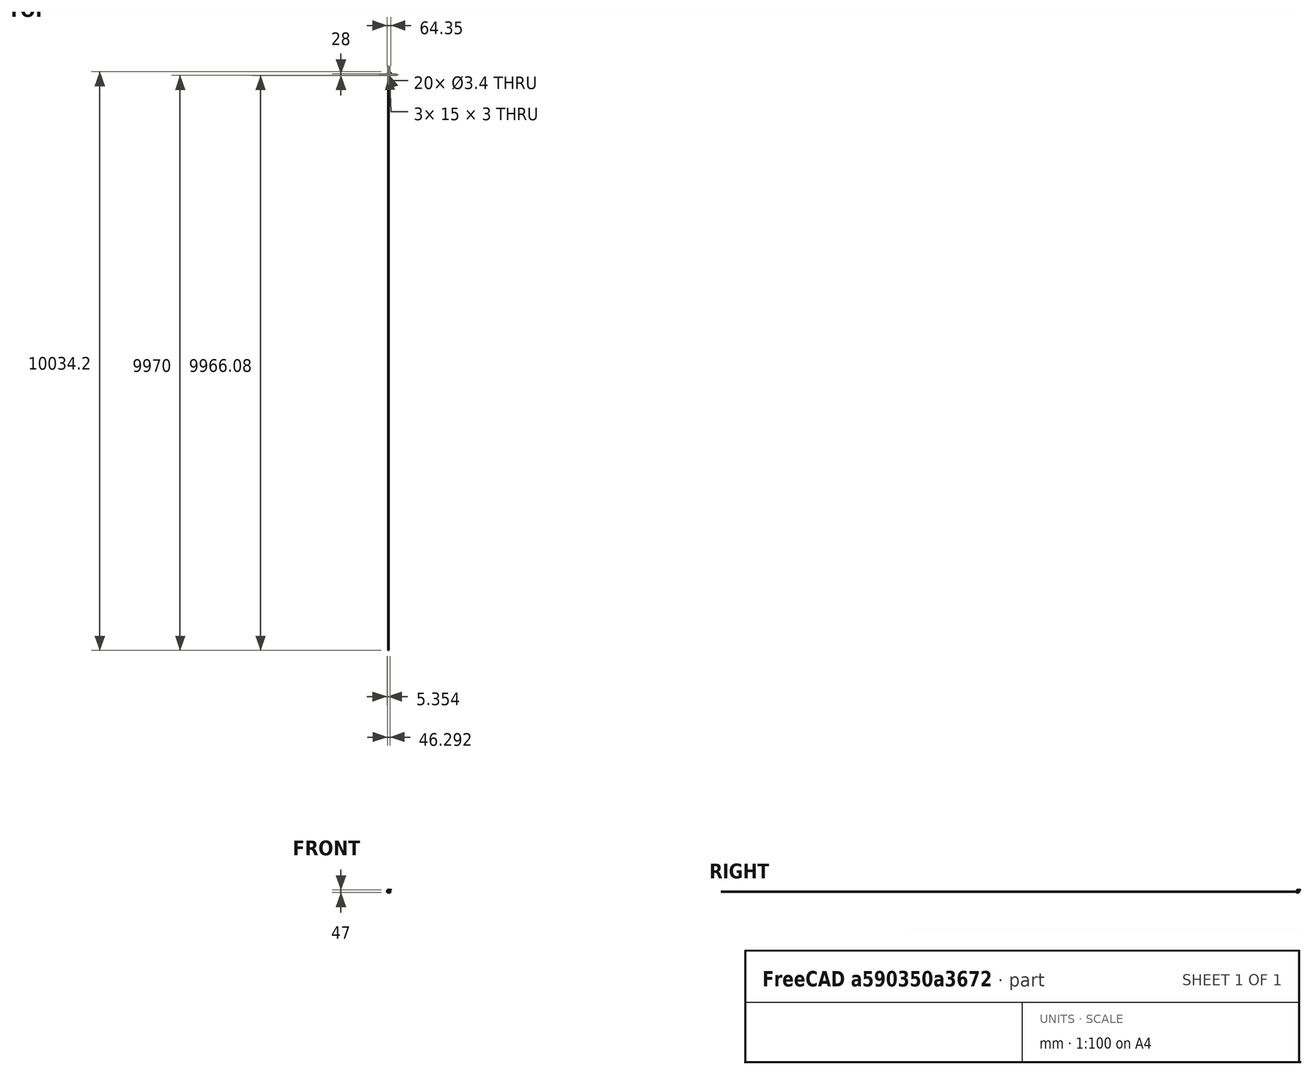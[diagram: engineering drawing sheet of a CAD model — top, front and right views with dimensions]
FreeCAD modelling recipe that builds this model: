
FCSTD DOCUMENT  (FreeCAD 0.14R2935 (Git))
Label: cabeza_v2
License: CC-BY 3.0
LicenseURL: http://creativecommons.org/licenses/by/3.0/
objects: Sketcher::SketchObject×22, PartDesign::Pocket×15, PartDesign::Pad×8, PartDesign::Chamfer×8, PartDesign::Fillet×6, App::DocumentObjectGroup×5, Part::Box×4, Part::FeaturePython×3, Part::Feature×3, Part::Cylinder×1, Mesh::Feature×1, Part::Cut×1
note: 94 computed .brp shape members not serialized (recipe doc carries the construction recipe); baked Part::Feature solids carry a one-line shape summary decoded from their .brp

FEATURE [Part::Box] Box
  Height = 2
  Length = 10
  Width = 12
FEATURE [Sketcher::SketchObject] Sketch
  Placement = pos=(0,0,2) rot=(0,0,1;0rad)
  Support = -> Box [Face6]
  sketch-geometry (1):
    g0: Circle CenterX=4.90431 CenterY=7.27272 CenterZ=0 NormalX=0 NormalY=0 NormalZ=1 Radius=4.25
  constraints (1):
    c: Radius(g0) = 4.25
FEATURE [PartDesign::Pad] Pad
  Length = 2
  Length2 = 100
  Sketch = -> Sketch
  Type = 0
FEATURE [Sketcher::SketchObject] Sketch001
  ExternalGeometry = -> [Pad]
  Placement = pos=(0,0,4) rot=(0,0,1;0rad)
  Support = -> Pad [Face8]
  sketch-geometry (1):
    g0: Circle CenterX=4.90431 CenterY=7.27272 CenterZ=0 NormalX=0 NormalY=0 NormalZ=1 Radius=2
  constraints (2):
    c: Coincident(g0,g-3)
    c: Radius(g0) = 2
FEATURE [PartDesign::Pocket] Pocket  label="camara"
  Length = 1
  Sketch = -> Sketch001
  Type = 0
FEATURE [App::DocumentObjectGroup] Grupo  label="Camera"
  Group = -> [Box,Pad,Pocket]
FEATURE [Part::FeaturePython] Clone  label="camara001"  # Draft clone (typed FeaturePython)
  Objects = -> [Pocket]
  Placement = pos=(1.5,0,-16) rot=(0,0,1;0rad)
  Scale = (1,1,1)
FEATURE [Part::Cylinder] Cylinder
  Angle = 360
  Height = 2
  Radius = 11.5
FEATURE [Sketcher::SketchObject] Sketch002
  Placement = pos=(0,0,2) rot=(0,0,1;0rad)
  Support = -> Cylinder [Face2]
  sketch-geometry (6):
    g0: LineSegment StartX=-3 StartY=3 StartZ=0 EndX=3 EndY=3 EndZ=0
    g1: LineSegment StartX=3 StartY=3 StartZ=0 EndX=3 EndY=-3 EndZ=0
    g2: LineSegment StartX=3 StartY=-3 StartZ=0 EndX=-3 EndY=-3 EndZ=0
    g3: LineSegment StartX=-3 StartY=-3 StartZ=0 EndX=-3 EndY=3 EndZ=0
    g4: LineSegment [constr] StartX=-3 StartY=3 StartZ=0 EndX=3 EndY=-3 EndZ=0
    g5: LineSegment [constr] StartX=3 StartY=3 StartZ=0 EndX=-3 EndY=-3 EndZ=0
  constraints (16):
    c: Coincident(g0,g1)
    c: Coincident(g1,g2)
    c: Coincident(g2,g3)
    c: Coincident(g3,g0)
    c: Horizontal(g0)
    c: Horizontal(g2)
    c: Vertical(g1)
    c: Vertical(g3)
    c: Equal(g0,g1)
    c: DistanceX(g2) = -6
    c: Coincident(g5,g0)
    c: Coincident(g5,g2)
    c: Coincident(g4,g1)
    c: Coincident(g4,g0)
    c: PointOnObject(g-1,g5)
    c: PointOnObject(g-1,g4)
FEATURE [PartDesign::Pad] Pad001
  Length = 1
  Length2 = 100
  Sketch = -> Sketch002
  Type = 0
FEATURE [Sketcher::SketchObject] Sketch003
  Placement = pos=(0,0,3) rot=(0,0,1;0rad)
  Support = -> Pad001 [Face8]
  sketch-geometry (1):
    g0: Circle CenterX=0 CenterY=0 CenterZ=0 NormalX=0 NormalY=0 NormalZ=1 Radius=2
  constraints (2):
    c: Coincident(g0,g-1)
    c: Radius(g0) = 2
FEATURE [PartDesign::Pocket] Pocket001
  Length = 1
  Sketch = -> Sketch003
  Type = 0
FEATURE [Sketcher::SketchObject] Sketch004
  ExternalGeometry = -> [Pocket001]
  Placement = pos=(0,0,2) rot=(0,0,1;0rad)
  Support = -> Pocket001 [Face2]
  sketch-geometry (28):
    g0: LineSegment StartX=-3 StartY=9.7 StartZ=0 EndX=3 EndY=9.7 EndZ=0
    g1: LineSegment StartX=3 StartY=9.7 StartZ=0 EndX=3 EndY=3.7 EndZ=0
    g2: LineSegment StartX=3 StartY=3.7 StartZ=0 EndX=-3 EndY=3.7 EndZ=0
    g3: LineSegment StartX=-3 StartY=3.7 StartZ=0 EndX=-3 EndY=9.7 EndZ=0
    g4: LineSegment StartX=-9.7 StartY=3 StartZ=0 EndX=-3.7 EndY=3 EndZ=0
    g5: LineSegment StartX=-3.7 StartY=3 StartZ=0 EndX=-3.7 EndY=-3 EndZ=0
    g6: LineSegment StartX=-3.7 StartY=-3 StartZ=0 EndX=-9.7 EndY=-3 EndZ=0
    g7: LineSegment StartX=-9.7 StartY=-3 StartZ=0 EndX=-9.7 EndY=3 EndZ=0
    g8: LineSegment StartX=-3 StartY=-3.7 StartZ=0 EndX=3 EndY=-3.7 EndZ=0
    g9: LineSegment StartX=3 StartY=-3.7 StartZ=0 EndX=3 EndY=-9.7 EndZ=0
    g10: LineSegment StartX=3 StartY=-9.7 StartZ=0 EndX=-3 EndY=-9.7 EndZ=0
    g11: LineSegment StartX=-3 StartY=-9.7 StartZ=0 EndX=-3 EndY=-3.7 EndZ=0
    g12: LineSegment StartX=3.7 StartY=3 StartZ=0 EndX=9.7 EndY=3 EndZ=0
    g13: LineSegment StartX=9.7 StartY=3 StartZ=0 EndX=9.7 EndY=-3 EndZ=0
    g14: LineSegment StartX=9.7 StartY=-3 StartZ=0 EndX=3.7 EndY=-3 EndZ=0
    g15: LineSegment StartX=3.7 StartY=-3 StartZ=0 EndX=3.7 EndY=3 EndZ=0
    g16: LineSegment [constr] StartX=-3 StartY=9.7 StartZ=0 EndX=3 EndY=3.7 EndZ=0
    g17: LineSegment [constr] StartX=3 StartY=9.7 StartZ=0 EndX=-3 EndY=3.7 EndZ=0
    g18: LineSegment [constr] StartX=3.7 StartY=3 StartZ=0 EndX=9.7 EndY=-3 EndZ=0
    g19: LineSegment [constr] StartX=9.7 StartY=3 StartZ=0 EndX=3.7 EndY=-3 EndZ=0
    g20: LineSegment [constr] StartX=-9.7 StartY=3 StartZ=0 EndX=-3.7 EndY=-3 EndZ=0
    g21: LineSegment [constr] StartX=-3.7 StartY=3 StartZ=0 EndX=-9.7 EndY=-3 EndZ=0
    g22: LineSegment [constr] StartX=-3 StartY=-3.7 StartZ=0 EndX=3 EndY=-9.7 EndZ=0
    g23: LineSegment [constr] StartX=3 StartY=-3.7 StartZ=0 EndX=-3 EndY=-9.7 EndZ=0
    g24: GeomPoint [constr] X=0 Y=-6.7 Z=0
    g25: GeomPoint [constr] X=6.7 Y=0 Z=0
    g26: GeomPoint [constr] X=-6.7 Y=0 Z=0
    g27: GeomPoint [constr] X=0 Y=6.7 Z=0
  constraints (72):
    c: Coincident(g0,g1)
    c: Coincident(g1,g2)
    c: Coincident(g2,g3)
    c: Coincident(g3,g0)
    c: Horizontal(g0)
    c: Horizontal(g2)
    c: Vertical(g1)
    c: Vertical(g3)
    c: Equal(g3,g2)
    c: Equal(g2,g-3)
    c: Coincident(g4,g5)
    c: Coincident(g5,g6)
    c: Coincident(g6,g7)
    c: Coincident(g7,g4)
    c: Horizontal(g4)
    c: Horizontal(g6)
    c: Vertical(g5)
    c: Vertical(g7)
    c: Coincident(g8,g9)
    c: Coincident(g9,g10)
    c: Coincident(g10,g11)
    c: Coincident(g11,g8)
    c: Horizontal(g8)
    c: Horizontal(g10)
    c: Vertical(g9)
    c: Vertical(g11)
    c: Coincident(g12,g13)
    c: Coincident(g13,g14)
    c: Coincident(g14,g15)
    c: Coincident(g15,g12)
    c: Horizontal(g12)
    c: Horizontal(g14)
    c: Vertical(g13)
    c: Vertical(g15)
    c: Equal(g12,g15)
    c: Equal(g15,g8)
    c: Equal(g8,g9)
    c: Equal(g9,g6)
    c: Equal(g6,g5)
    c: Equal(g2,g12)
    c: Coincident(g23,g10)
    c: Coincident(g22,g8)
    c: Coincident(g23,g8)
    c: Coincident(g22,g9)
    c: PointOnObject(g24,g-2)
    c: PointOnObject(g24,g23)
    c: PointOnObject(g24,g22)
    c: Coincident(g19,g12)
    c: Coincident(g18,g13)
    c: Coincident(g18,g12)
    c: Coincident(g19,g14)
    c: Coincident(g16,g1)
    c: Coincident(g17,g0)
    c: Coincident(g17,g2)
    c: Coincident(g16,g0)
    c: Coincident(g21,g4)
    c: Coincident(g20,g4)
    c: Coincident(g21,g6)
    c: Coincident(g20,g5)
    c: PointOnObject(g25,g-1)
    c: PointOnObject(g26,g-1)
    c: PointOnObject(g27,g-2)
    c: PointOnObject(g26,g20)
    c: PointOnObject(g26,g21)
    c: PointOnObject(g25,g19)
    c: PointOnObject(g25,g18)
    c: PointOnObject(g27,g16)
    c: PointOnObject(g27,g17)
    c: Distance(g-4,g4) = 0.7
    c: Distance(g-4,g8) = 0.7
    c: Distance(g-5,g14) = 0.7
    c: Distance(g2,g-4) = 0.7
FEATURE [PartDesign::Pad] Pad002
  Length = 1
  Length2 = 100
  Sketch = -> Sketch004
  Type = 0
FEATURE [Sketcher::SketchObject] Sketch005
  ExternalGeometry = -> [Pad002]
  Placement = pos=(0,0,3) rot=(0,0,1;0rad)
  Support = -> Pad002 [Face26]
  sketch-geometry (4):
    g0: Circle CenterX=0 CenterY=6.61559 CenterZ=0 NormalX=0 NormalY=0 NormalZ=1 Radius=2
    g1: Circle CenterX=-6.61558 CenterY=0 CenterZ=0 NormalX=0 NormalY=0 NormalZ=1 Radius=2
    g2: Circle CenterX=6.71215 CenterY=0 CenterZ=0 NormalX=0 NormalY=0 NormalZ=1 Radius=2
    g3: Circle CenterX=0 CenterY=-6.71214 CenterZ=0 NormalX=0 NormalY=0 NormalZ=1 Radius=2
  constraints (8):
    c: Equal(g1,g0)
    c: Equal(g0,g-3)
    c: Equal(g-3,g2)
    c: Equal(g2,g3)
    c: PointOnObject(g2,g-1)
    c: PointOnObject(g0,g-2)
    c: PointOnObject(g1,g-1)
    c: PointOnObject(g3,g-2)
FEATURE [PartDesign::Pocket] Pocket002
  Length = 1
  Sketch = -> Sketch005
  Type = 0
FEATURE [Part::FeaturePython] Clone001  label="ojo001"  # Draft clone (typed FeaturePython)
  Objects = -> [Pocket002]
  Placement = pos=(-7,-6,-13) rot=(0,0,1;0rad)
  Scale = (1,1,1)
FEATURE [App::DocumentObjectGroup] Grupo001  label="ojo"
  Group = -> [Cylinder,Pad001,Pocket001,Pad002,Pocket002]
FEATURE [Part::FeaturePython] Clone002  label="ojo002"  # Draft clone (typed FeaturePython)
  Objects = -> [Pocket002]
  Placement = pos=(21,-7,-13) rot=(0,0,1;0rad)
  Scale = (1,1,1)
FEATURE [Part::Box] Box001
  Height = 4
  Length = 35
  Placement = pos=(-11,-31,-17) rot=(0,0,1;0rad)
  Width = 47
FEATURE [Mesh::Feature] _g_servo  label="9g_servo"
  Placement = pos=(0,-7,-24) rot=(0.57735,0.57735,0.57735;2.0944rad)
FEATURE [Sketcher::SketchObject] Sketch006
  ExternalGeometry = -> [Box001]
  Placement = pos=(-11,-31,-17) rot=(1,0,0;3.14159rad)
  Support = -> Box001 [Face5]
  sketch-geometry (9):
    g0: LineSegment StartX=6.5 StartY=-7.91944 StartZ=0 EndX=13.302 EndY=-7.91944 EndZ=0
    g1: LineSegment StartX=13.302 StartY=-7.91944 StartZ=0 EndX=13.302 EndY=-11.9194 EndZ=0
    g2: LineSegment StartX=13.302 StartY=-11.9194 StartZ=0 EndX=6.5 EndY=-11.9194 EndZ=0
    g3: LineSegment StartX=6.5 StartY=-11.9194 StartZ=0 EndX=6.5 EndY=-7.91944 EndZ=0
    g4: LineSegment StartX=6.5 StartY=-35.9194 StartZ=0 EndX=13.302 EndY=-35.9194 EndZ=0
    g5: LineSegment StartX=13.302 StartY=-35.9194 StartZ=0 EndX=13.302 EndY=-39.9194 EndZ=0
    g6: LineSegment StartX=13.302 StartY=-39.9194 StartZ=0 EndX=6.5 EndY=-39.9194 EndZ=0
    g7: LineSegment StartX=6.5 StartY=-39.9194 StartZ=0 EndX=6.5 EndY=-35.9194 EndZ=0
    g8: LineSegment [constr] StartX=6.5 StartY=0 StartZ=0 EndX=6.5 EndY=-47 EndZ=0
  constraints (27):
    c: Coincident(g0,g1)
    c: Coincident(g1,g2)
    c: Coincident(g2,g3)
    c: Coincident(g3,g0)
    c: Horizontal(g0)
    c: Horizontal(g2)
    c: Vertical(g1)
    c: Vertical(g3)
    c: Coincident(g4,g5)
    c: Coincident(g5,g6)
    c: Coincident(g6,g7)
    c: Coincident(g7,g4)
    c: Horizontal(g4)
    c: Horizontal(g6)
    c: Vertical(g5)
    c: Vertical(g7)
    c: Equal(g2,g4)
    c: Vertical(g8)
    c: PointOnObject(g8,g-3)
    c: PointOnObject(g8,g-1)
    c: PointOnObject(g0,g8)
    c: PointOnObject(g4,g8)
    c: Equal(g1,g5)
    c: DistanceY(g1) = -4
    c: Distance(g2,g4) = 24
    c: Distance(g6,g8) = 7.08056
    c: Distance(g-3,g8) = 6.5
FEATURE [PartDesign::Pad] Pad003
  Length = 14
  Length2 = 100
  Placement = pos=(-11,-31,-17) rot=(0,0,1;0rad)
  Sketch = -> Sketch006
  Type = 0
FEATURE [Sketcher::SketchObject] Sketch007
  ExternalGeometry = -> [Pad003]
  Placement = pos=(2.30204,-31,-17) rot=(0.57735,0.57735,0.57735;2.0944rad)
  Support = -> Pad003 [Face7]
  sketch-geometry (3):
    g0: Circle CenterX=9.93523 CenterY=-7.03791 CenterZ=0 NormalX=0 NormalY=0 NormalZ=1 Radius=1.64716
    g1: Circle CenterX=37.8885 CenterY=-7.03791 CenterZ=0 NormalX=0 NormalY=0 NormalZ=1 Radius=1.53113
    g2: LineSegment [constr] StartX=35.9194 StartY=-7.03791 StartZ=0 EndX=11.9194 EndY=-7.03791 EndZ=0
  constraints (5):
    c: PointOnObject(g2,g-3)
    c: Horizontal(g2)
    c: PointOnObject(g2,g-4)
    c: PointOnObject(g0,g2)
    c: PointOnObject(g1,g2)
FEATURE [PartDesign::Pocket] Pocket003
  Length = 7
  Placement = pos=(-11,-31,-17) rot=(0,0,1;0rad)
  Sketch = -> Sketch007
  Type = 0
FEATURE [Sketcher::SketchObject] Sketch008
  ExternalGeometry = -> [Pocket003]
  Placement = pos=(-11,-31,-17) rot=(1,0,0;3.14159rad)
  Support = -> Pocket003 [Face5]
  sketch-geometry (6):
    g0: ArcOfCircle CenterX=31.6459 CenterY=-23.9498 CenterZ=0 NormalX=0 NormalY=0 NormalZ=1 Radius=11.5 StartAngle=5.00835 EndAngle=7.55802
    g1: LineSegment [constr] StartX=35 StartY=-12.9498 StartZ=0 EndX=0 EndY=-12.9498 EndZ=0
    g2: LineSegment [constr] StartX=35 StartY=-34.9498 StartZ=0 EndX=0 EndY=-34.9498 EndZ=0
    g3: ArcOfCircle CenterX=3.3541 CenterY=-23.9498 CenterZ=0 NormalX=0 NormalY=0 NormalZ=1 Radius=11.5 StartAngle=1.86676 EndAngle=4.41643
    g4: LineSegment StartX=35 StartY=-12.9498 StartZ=0 EndX=35 EndY=-34.9498 EndZ=0
    g5: LineSegment StartX=0 StartY=-12.9498 StartZ=0 EndX=0 EndY=-34.9498 EndZ=0
  constraints (20):
    c: PointOnObject(g0,g-3)
    c: PointOnObject(g0,g-3)
    c: Distance(g0,g0) = 22
    c: Radius(g0) = 11.5
    c: Horizontal(g1)
    c: Horizontal(g2)
    c: Distance(g-3,g0) = 12.9498
    c: Coincident(g1,g0)
    c: PointOnObject(g1,g-2)
    c: Coincident(g2,g0)
    c: PointOnObject(g2,g-2)
    c: Coincident(g3,g2)
    c: Coincident(g3,g1)
    c: Equal(g0,g3)
    c: Vertical(g4)
    c: Coincident(g4,g0)
    c: Coincident(g4,g0)
    c: Vertical(g5)
    c: Coincident(g5,g1)
    c: Coincident(g5,g2)
FEATURE [PartDesign::Pad] Pad004
  Length = 4
  Length2 = 100
  Placement = pos=(-11,-31,-17) rot=(0,0,1;0rad)
  Reversed = true
  Sketch = -> Sketch008
  Type = 0
FEATURE [Sketcher::SketchObject] Sketch009
  ExternalGeometry = -> [Pad004]
  Placement = pos=(-11,-31,-13) rot=(0,0,1;0rad)
  Support = -> Pad004 [Face4]
  sketch-geometry (6):
    g0: Circle CenterX=17.5 CenterY=38.5843 CenterZ=0 NormalX=0 NormalY=0 NormalZ=1 Radius=4.5
    g1: LineSegment [constr] StartX=0 StartY=38.5843 StartZ=0 EndX=17.5 EndY=38.5843 EndZ=0
    g2: LineSegment [constr] StartX=17.5 StartY=38.5843 StartZ=0 EndX=35 EndY=38.5843 EndZ=0
    g3: Circle CenterX=-5.6459 CenterY=23.9498 CenterZ=0 NormalX=0 NormalY=0 NormalZ=1 Radius=1.7
    g4: Circle CenterX=40.6459 CenterY=23.9498 CenterZ=0 NormalX=0 NormalY=0 NormalZ=1 Radius=1.7
    g5: LineSegment [constr] StartX=-8.1459 StartY=23.9498 StartZ=0 EndX=43.1459 EndY=23.9498 EndZ=0
  constraints (19):
    c: Horizontal(g1)
    c: Horizontal(g2)
    c: PointOnObject(g1,g-2)
    c: PointOnObject(g2,g-3)
    c: Coincident(g2,g0)
    c: Coincident(g1,g0)
    c: Equal(g1,g2)
    c: Radius(g0) = 4.5
    c: DistanceY(g-1,g2) = 38.5843
    c: Horizontal(g5)
    c: PointOnObject(g5,g-5)
    c: PointOnObject(g5,g-4)
    c: PointOnObject(g3,g5)
    c: PointOnObject(g4,g5)
    c: Radius(g4) = 1.7
    c: Radius(g3) = 1.7
    c: Distance(g3,g5) = 2.5
    c: Distance(g4,g5) = 2.5
    c: PointOnObject(g-5,g5)
FEATURE [PartDesign::Pocket] Pocket004
  Length = 4
  Placement = pos=(-11,-31,-17) rot=(0,0,1;0rad)
  Sketch = -> Sketch009
  Type = 0
FEATURE [Part::Feature] Pocket004001  label="Pocket005"
  shape: bbox 51.29 x 47 x 18 mm, 26 faces (baked)
FEATURE [PartDesign::Chamfer] Chamfer
  Base = -> Pocket004001 [Edge6]
  Size = 10
FEATURE [PartDesign::Chamfer] Chamfer001
  Base = -> Chamfer [Edge3]
  Size = 10
FEATURE [PartDesign::Fillet] Fillet
  Base = -> Chamfer001 [Edge3]
  Radius = 10
FEATURE [PartDesign::Fillet] Fillet001
  Base = -> Fillet [Edge3]
  Radius = 10
FEATURE [PartDesign::Fillet] Fillet002
  Base = -> Fillet001 [Edge45]
  Radius = 3
FEATURE [PartDesign::Fillet] Fillet003
  Base = -> Fillet002 [Edge43]
  Radius = 3
FEATURE [PartDesign::Chamfer] Chamfer002
  Base = -> Fillet003 [Edge46]
  Size = 10
FEATURE [PartDesign::Chamfer] Chamfer003
  Base = -> Chamfer002 [Edge29]
  Size = 10
FEATURE [Sketcher::SketchObject] Sketch010
  ExternalGeometry = -> [Chamfer003]
  Placement = pos=(0,0,-13) rot=(0,0,1;0rad)
  Support = -> Chamfer003 [Face29]
  sketch-geometry (9):
    g0: LineSegment [constr] StartX=-16.6459 StartY=-7.0502 StartZ=0 EndX=29.6459 EndY=-7.0502 EndZ=0
    g1: Circle CenterX=3.3541 CenterY=-7.0502 CenterZ=0 NormalX=0 NormalY=0 NormalZ=1 Radius=1.7
    g2: Circle CenterX=9.6459 CenterY=-7.0502 CenterZ=0 NormalX=0 NormalY=0 NormalZ=1 Radius=1.7
    g3: LineSegment [constr] StartX=-1 StartY=-7.0502 StartZ=0 EndX=-1 EndY=-31 EndZ=0
    g4: LineSegment [constr] StartX=14 StartY=-7.0502 StartZ=0 EndX=14 EndY=-31 EndZ=0
    g5: LineSegment StartX=-1 StartY=-23.5 StartZ=0 EndX=14 EndY=-23.5 EndZ=0
    g6: LineSegment StartX=14 StartY=-23.5 StartZ=0 EndX=14 EndY=-26.5 EndZ=0
    g7: LineSegment StartX=14 StartY=-26.5 StartZ=0 EndX=-1 EndY=-26.5 EndZ=0
    g8: LineSegment StartX=-1 StartY=-26.5 StartZ=0 EndX=-1 EndY=-23.5 EndZ=0
  constraints (27):
    c: Horizontal(g0)
    c: Coincident(g0,g-4)
    c: Coincident(g0,g-3)
    c: PointOnObject(g1,g0)
    c: PointOnObject(g2,g0)
    c: Radius(g2) = 1.7
    c: Radius(g1) = 1.7
    c: Distance(g0,g1) = 20
    c: Distance(g2,g0) = 20
    c: Vertical(g3)
    c: Coincident(g3,g-5)
    c: PointOnObject(g3,g0)
    c: Vertical(g4)
    c: Coincident(g4,g-5)
    c: PointOnObject(g4,g0)
    c: Coincident(g5,g6)
    c: Coincident(g6,g7)
    c: Coincident(g7,g8)
    c: Coincident(g8,g5)
    c: Horizontal(g5)
    c: Horizontal(g7)
    c: Vertical(g6)
    c: Vertical(g8)
    c: DistanceY(g6) = -3
    c: PointOnObject(g7,g3)
    c: PointOnObject(g6,g4)
    c: Distance(g7,g3) = 4.5
FEATURE [PartDesign::Pocket] Pocket004002
  Length = 5
  Sketch = -> Sketch010
  Type = 0
FEATURE [Sketcher::SketchObject] Sketch011
  Placement = pos=(0,8.91944,0) rot=(0,0.707107,0.707107;3.14159rad)
  Support = -> Pocket004002 [Face18]
  sketch-geometry (4):
    g0: LineSegment StartX=-1.74892 StartY=-26.7435 StartZ=0 EndX=3.95108 EndY=-26.7435 EndZ=0
    g1: LineSegment StartX=3.95108 StartY=-26.7435 StartZ=0 EndX=3.95108 EndY=-29.3435 EndZ=0
    g2: LineSegment StartX=3.95108 StartY=-29.3435 StartZ=0 EndX=-1.74892 EndY=-29.3435 EndZ=0
    g3: LineSegment StartX=-1.74892 StartY=-29.3435 StartZ=0 EndX=-1.74892 EndY=-26.7435 EndZ=0
  constraints (10):
    c: Coincident(g0,g1)
    c: Coincident(g1,g2)
    c: Coincident(g2,g3)
    c: Coincident(g3,g0)
    c: Horizontal(g0)
    c: Horizontal(g2)
    c: Vertical(g1)
    c: Vertical(g3)
    c: DistanceY(g1) = -2.6
    c: DistanceX(g2) = -5.7
FEATURE [PartDesign::Pocket] Pocket004003
  Length = 5
  Sketch = -> Sketch011
  Type = 1
FEATURE [Sketcher::SketchObject] Sketch012
  ExternalGeometry = -> [Pocket004003]
  Placement = pos=(0,0,-31) rot=(1,0,0;3.14159rad)
  Support = -> Pocket004003 [Face37]
  sketch-geometry (6):
    g0: LineSegment [constr] StartX=-4.5 StartY=23.0806 StartZ=0 EndX=2.30204 EndY=19.0806 EndZ=0
    g1: LineSegment [constr] StartX=2.30204 StartY=23.0806 StartZ=0 EndX=-4.5 EndY=19.0806 EndZ=0
    g2: Circle CenterX=-1.09898 CenterY=21.0806 CenterZ=0 NormalX=0 NormalY=0 NormalZ=1 Radius=1.7
    g3: LineSegment [constr] StartX=-4.5 StartY=-4.91944 StartZ=0 EndX=2.30204 EndY=-8.91944 EndZ=0
    g4: LineSegment [constr] StartX=2.30204 StartY=-4.91944 StartZ=0 EndX=-4.5 EndY=-8.91944 EndZ=0
    g5: Circle CenterX=-1.09898 CenterY=-6.91944 CenterZ=0 NormalX=0 NormalY=0 NormalZ=1 Radius=1.7
  constraints (14):
    c: Coincident(g1,g-4)
    c: Coincident(g1,g-3)
    c: Coincident(g0,g-4)
    c: Coincident(g0,g-3)
    c: PointOnObject(g2,g1)
    c: PointOnObject(g2,g0)
    c: Radius(g2) = 1.7
    c: Coincident(g4,g-6)
    c: Coincident(g4,g-5)
    c: Coincident(g3,g-6)
    c: Coincident(g3,g-5)
    c: PointOnObject(g5,g4)
    c: PointOnObject(g5,g3)
    c: Radius(g5) = 1.7
FEATURE [PartDesign::Pocket] Pocket004004
  Length = 4
  Sketch = -> Sketch012
  Type = 0
FEATURE [Part::Box] Box002
  Height = 26
  Length = 36
  Placement = pos=(-12,-31,-43) rot=(0,0,1;0rad)
  Width = 47
FEATURE [PartDesign::Pocket] Pocket004005
  Length = 4
  Sketch = -> Sketch012
  Type = 0
FEATURE [Part::Feature] Pocket004006  label="cara"
  shape: bbox 51.29 x 47 x 18 mm, 50 faces (baked)
FEATURE [PartDesign::Fillet] Fillet004
  Base = -> Box002 [Edge7]
  Placement = pos=(-12,-31,-43) rot=(0,0,1;0rad)
  Radius = 17
FEATURE [PartDesign::Fillet] Fillet005
  Base = -> Fillet004 [Edge15]
  Placement = pos=(-12,-31,-43) rot=(0,0,1;0rad)
  Radius = 17
FEATURE [PartDesign::Chamfer] Chamfer004
  Base = -> Fillet005 [Edge16]
  Placement = pos=(-12,-31,-43) rot=(0,0,1;0rad)
  Size = 10
FEATURE [PartDesign::Chamfer] Chamfer005
  Base = -> Chamfer004 [Edge16]
  Placement = pos=(-12,-31,-43) rot=(0,0,1;0rad)
  Size = 10
FEATURE [Part::Box] Box003
  Height = 26
  Length = 36
  Placement = pos=(-12,-31,-43) rot=(0,0,1;0rad)
  Width = 10
FEATURE [Part::Cut] Cut
  Base = -> Chamfer005
  Tool = -> Box003
FEATURE [Sketcher::SketchObject] Sketch013
  ExternalGeometry = -> [Cut]
  Placement = pos=(0,-21,0) rot=(1,0,0;1.5708rad)
  Support = -> Cut [Face7]
  sketch-geometry (4):
    g0: LineSegment StartX=-9 StartY=-17 StartZ=0 EndX=21 EndY=-17 EndZ=0
    g1: LineSegment StartX=21 StartY=-17 StartZ=0 EndX=21 EndY=-40 EndZ=0
    g2: LineSegment StartX=21 StartY=-40 StartZ=0 EndX=-9 EndY=-40 EndZ=0
    g3: LineSegment StartX=-9 StartY=-40 StartZ=0 EndX=-9 EndY=-17 EndZ=0
  constraints (12):
    c: Coincident(g0,g1)
    c: Coincident(g1,g2)
    c: Coincident(g2,g3)
    c: Coincident(g3,g0)
    c: Horizontal(g0)
    c: Horizontal(g2)
    c: Vertical(g1)
    c: Vertical(g3)
    c: PointOnObject(g0,g-5)
    c: Distance(g-5,g0) = 3
    c: Distance(g-5,g0) = 3
    c: Distance(g2,g-6) = 3
FEATURE [PartDesign::Pocket] Pocket004007
  Length = 27
  Sketch = -> Sketch013
  Type = 0
FEATURE [Sketcher::SketchObject] Sketch014
  ExternalGeometry = -> [Pocket004007]
  Placement = pos=(0,0,-17) rot=(0,0,1;0rad)
  Support = -> Pocket004007 [Face1]
  sketch-geometry (4):
    g0: LineSegment StartX=-0.588067 StartY=13.0845 StartZ=0 EndX=12.9735 EndY=13.0845 EndZ=0
    g1: LineSegment StartX=12.9735 StartY=13.0845 StartZ=0 EndX=12.9735 EndY=6 EndZ=0
    g2: LineSegment StartX=12.9735 StartY=6 StartZ=0 EndX=-0.588067 EndY=6 EndZ=0
    g3: LineSegment StartX=-0.588067 StartY=6 StartZ=0 EndX=-0.588067 EndY=13.0845 EndZ=0
  constraints (9):
    c: Coincident(g0,g1)
    c: Coincident(g1,g2)
    c: Coincident(g2,g3)
    c: Coincident(g3,g0)
    c: Horizontal(g0)
    c: Horizontal(g2)
    c: Vertical(g1)
    c: Vertical(g3)
    c: PointOnObject(g2,g-3)
FEATURE [PartDesign::Pocket] Pocket004008
  Length = 23
  Sketch = -> Sketch014
  Type = 0
FEATURE [Sketcher::SketchObject] Sketch015
  ExternalGeometry = -> [Pocket004008]
  Placement = pos=(0,0,-43) rot=(1,0,0;3.14159rad)
  Support = -> Pocket004008 [Face15]
  sketch-geometry (8):
    g0: LineSegment StartX=-22 StartY=21 StartZ=0 EndX=-12 EndY=21 EndZ=0
    g1: LineSegment StartX=-12 StartY=21 StartZ=0 EndX=-12 EndY=1 EndZ=0
    g2: LineSegment StartX=-12 StartY=1 StartZ=0 EndX=-22 EndY=1 EndZ=0
    g3: LineSegment StartX=-22 StartY=1 StartZ=0 EndX=-22 EndY=21 EndZ=0
    g4: LineSegment StartX=34 StartY=21 StartZ=0 EndX=24 EndY=21 EndZ=0
    g5: LineSegment StartX=24 StartY=21 StartZ=0 EndX=24 EndY=1 EndZ=0
    g6: LineSegment StartX=24 StartY=1 StartZ=0 EndX=34 EndY=1 EndZ=0
    g7: LineSegment StartX=34 StartY=1 StartZ=0 EndX=34 EndY=21 EndZ=0
  constraints (22):
    c: Coincident(g0,g1)
    c: Coincident(g1,g2)
    c: Coincident(g2,g3)
    c: Coincident(g3,g0)
    c: Horizontal(g0)
    c: Horizontal(g2)
    c: Vertical(g1)
    c: Vertical(g3)
    c: Coincident(g-3,g0)
    c: Coincident(g1,g-3)
    c: Coincident(g4,g5)
    c: Coincident(g5,g6)
    c: Coincident(g6,g7)
    c: Coincident(g7,g4)
    c: Horizontal(g4)
    c: Horizontal(g6)
    c: Vertical(g5)
    c: Vertical(g7)
    c: Coincident(g5,g-4)
    c: Coincident(g4,g-4)
    c: Equal(g0,g4)
    c: DistanceX(g2) = -10
FEATURE [PartDesign::Pad] Pad005
  Length = 25
  Length2 = 100
  Reversed = true
  Sketch = -> Sketch015
  Type = 0
FEATURE [PartDesign::Chamfer] Chamfer006
  Base = -> Pad005 [Edge48]
  Size = 9
FEATURE [PartDesign::Chamfer] Chamfer007
  Base = -> Chamfer006 [Edge67]
  Size = 9
FEATURE [Sketcher::SketchObject] Sketch016
  ExternalGeometry = -> [Chamfer007]
  Placement = pos=(2.5,0,-2.5) rot=(0.357407,-0.357407,-0.862856;1.71777rad)
  Support = -> Chamfer007 [Face21]
  sketch-geometry (4):
    g0: LineSegment StartX=4 StartY=-28.1482 StartZ=0 EndX=19 EndY=-28.1482 EndZ=0
    g1: LineSegment StartX=19 StartY=-28.1482 StartZ=0 EndX=19 EndY=-31.1482 EndZ=0
    g2: LineSegment StartX=19 StartY=-31.1482 StartZ=0 EndX=4 EndY=-31.1482 EndZ=0
    g3: LineSegment StartX=4 StartY=-31.1482 StartZ=0 EndX=4 EndY=-28.1482 EndZ=0
  constraints (12):
    c: Coincident(g0,g1)
    c: Coincident(g1,g2)
    c: Coincident(g2,g3)
    c: Coincident(g3,g0)
    c: Horizontal(g0)
    c: Horizontal(g2)
    c: Vertical(g1)
    c: Vertical(g3)
    c: Distance(g2,g-3) = 3.5
    c: DistanceX(g2) = -15
    c: Distance(g1,g-4) = 2
    c: DistanceY(g1) = -3
FEATURE [PartDesign::Pocket] Pocket004009
  Length = 10
  Sketch = -> Sketch016
  Type = 0
FEATURE [Sketcher::SketchObject] Sketch017
  ExternalGeometry = -> [Pocket004009]
  Placement = pos=(3.5,0,3.5) rot=(0.357407,0.357407,0.862856;1.71777rad)
  Support = -> Pocket004009 [Face3]
  sketch-geometry (4):
    g0: LineSegment StartX=-18 StartY=-37.1335 StartZ=0 EndX=-3 EndY=-37.1335 EndZ=0
    g1: LineSegment StartX=-3 StartY=-37.1335 StartZ=0 EndX=-3 EndY=-40.1335 EndZ=0
    g2: LineSegment StartX=-3 StartY=-40.1335 StartZ=0 EndX=-18 EndY=-40.1335 EndZ=0
    g3: LineSegment StartX=-18 StartY=-40.1335 StartZ=0 EndX=-18 EndY=-37.1335 EndZ=0
  constraints (12):
    c: Coincident(g0,g1)
    c: Coincident(g1,g2)
    c: Coincident(g2,g3)
    c: Coincident(g3,g0)
    c: Horizontal(g0)
    c: Horizontal(g2)
    c: Vertical(g1)
    c: Vertical(g3)
    c: DistanceX(g2) = -15
    c: Distance(g0,g-3) = 3
    c: Distance(g2,g-4) = 3
    c: DistanceY(g1) = -3
FEATURE [PartDesign::Pocket] Pocket004010
  Length = 15
  Sketch = -> Sketch017
  Type = 0
FEATURE [Sketcher::SketchObject] Sketch018
  ExternalGeometry = -> [Pocket004010]
  Placement = pos=(0,16,0) rot=(0,0.707107,0.707107;3.14159rad)
  Support = -> Pocket004010 [Face24]
  sketch-geometry (4):
    g0: LineSegment StartX=-7 StartY=-17 StartZ=0 EndX=-5 EndY=-17 EndZ=0
    g1: LineSegment StartX=-5 StartY=-17 StartZ=0 EndX=-5 EndY=-43 EndZ=0
    g2: LineSegment StartX=-5 StartY=-43 StartZ=0 EndX=-7 EndY=-43 EndZ=0
    g3: LineSegment StartX=-7 StartY=-43 StartZ=0 EndX=-7 EndY=-17 EndZ=0
  constraints (11):
    c: Coincident(g0,g1)
    c: Coincident(g1,g2)
    c: Coincident(g2,g3)
    c: Coincident(g3,g0)
    c: Horizontal(g0)
    c: Horizontal(g2)
    c: Vertical(g1)
    c: Vertical(g3)
    c: Coincident(g1,g-4)
    c: Coincident(g0,g-4)
    c: Coincident(g0,g-3)
FEATURE [PartDesign::Pad] Pad006
  Length = 10
  Length2 = 100
  Sketch = -> Sketch018
  Type = 0
FEATURE [Sketcher::SketchObject] Sketch019
  ExternalGeometry = -> [Pad006]
  Placement = pos=(7,0,0) rot=(0.57735,0.57735,0.57735;2.0944rad)
  Support = -> Pad006 [Face35]
  sketch-geometry (3):
    g0: LineSegment StartX=16 StartY=-17 StartZ=0 EndX=26 EndY=-43 EndZ=0
    g1: LineSegment StartX=26 StartY=-43 StartZ=0 EndX=26 EndY=-17 EndZ=0
    g2: LineSegment StartX=26 StartY=-17 StartZ=0 EndX=16 EndY=-17 EndZ=0
  constraints (6):
    c: Coincident(g0,g1)
    c: Coincident(g1,g2)
    c: Coincident(g2,g0)
    c: Coincident(g1,g-4)
    c: Coincident(g0,g-3)
    c: Coincident(g0,g-4)
FEATURE [PartDesign::Pocket] Pocket004011  label="cabeza"
  Length = 5
  Sketch = -> Sketch019
  Type = 0
FEATURE [App::DocumentObjectGroup] Grupo002  label="craneo"
  Group = -> [Fillet004,Fillet005,Chamfer004,Cut,Pocket004007,Pocket004008,Pad005,Chamfer006,Chamfer007,Pocket004009,Pocket004010,Pad006,Pocket004011,Box002]
FEATURE [App::DocumentObjectGroup] Grupo003  label="Rostro"
  Group = -> [Pad003,Pocket003,Pad004,Pocket004,Pocket004001,Chamfer,Chamfer001,Fillet,Fillet001,Fillet002,Fillet003,Chamfer002,Chamfer003,Pocket004002,Pocket004003,Pocket004004,Pocket004005,Pocket004006,Box001]
FEATURE [App::DocumentObjectGroup] Grupo004  label="Montaje"
  Group = -> [Grupo,Clone,Clone001,Grupo001,Clone002,_g_servo]
FEATURE [Sketcher::SketchObject] Sketch020
  ExternalGeometry = -> [Pocket004006]
  Placement = pos=(0,0,-17) rot=(1,0,0;3.14159rad)
  Support = -> Pocket004006 [Face1]
  sketch-geometry (3):
    g0: LineSegment [constr] StartX=-16.6459 StartY=7.0502 StartZ=0 EndX=29.6459 EndY=7.0502 EndZ=0
    g1: Circle CenterX=-4.22957 CenterY=7.0502 CenterZ=0 NormalX=0 NormalY=0 NormalZ=1 Radius=5
    g2: Circle CenterX=17.4791 CenterY=7.0502 CenterZ=0 NormalX=0 NormalY=0 NormalZ=1 Radius=5
  constraints (6):
    c: Coincident(g0,g-3)
    c: Coincident(g0,g-4)
    c: PointOnObject(g1,g0)
    c: PointOnObject(g2,g0)
    c: Radius(g1) = 5
    c: Equal(g1,g2)
FEATURE [PartDesign::Pocket] Pocket004012
  Length = 5
  Sketch = -> Sketch020
  Type = 0
FEATURE [Sketcher::SketchObject] Sketch021
  ExternalGeometry = -> [Pocket004012]
  Placement = pos=(0,0,-17) rot=(1,0,0;3.14159rad)
  Support = -> Pocket004012 [Face1]
  sketch-geometry (6):
    g0: LineSegment StartX=-4.5 StartY=-4.91944 StartZ=0 EndX=-5.5 EndY=-4.91944 EndZ=0
    g1: LineSegment StartX=-5.5 StartY=-4.91944 StartZ=0 EndX=-5.5 EndY=-9.91944 EndZ=0
    g2: LineSegment StartX=-5.5 StartY=-9.91944 StartZ=0 EndX=2.20263 EndY=-9.91944 EndZ=0
    g3: LineSegment StartX=2.20263 StartY=-9.91944 StartZ=0 EndX=2.20263 EndY=-8.91944 EndZ=0
    g4: LineSegment StartX=2.20263 StartY=-8.91944 StartZ=0 EndX=-4.5 EndY=-8.91944 EndZ=0
    g5: LineSegment StartX=-4.5 StartY=-8.91944 StartZ=0 EndX=-4.5 EndY=-4.91944 EndZ=0
  constraints (17):
    c: Horizontal(g0)
    c: Coincident(g0,g1)
    c: Vertical(g1)
    c: Coincident(g1,g2)
    c: Horizontal(g2)
    c: Coincident(g2,g3)
    c: Coincident(g3,g4)
    c: Coincident(g4,g5)
    c: Vertical(g5)
    c: Coincident(g5,g0)
    c: Horizontal(g4)
    c: Vertical(g3)
    c: Coincident(g0,g-3)
    c: Coincident(g4,g-4)
    c: Coincident(g-4,g3)
    c: Distance(g3) = 1
    c: Distance(g0) = 1
FEATURE [PartDesign::Pad] Pad007
  Length = 14
  Length2 = 100
  Sketch = -> Sketch021
  Type = 0
FEATURE [Part::Feature] Pad007001  label="Pad008"
  shape: bbox 51.29 x 47 x 18 mm, 56 faces (baked)
